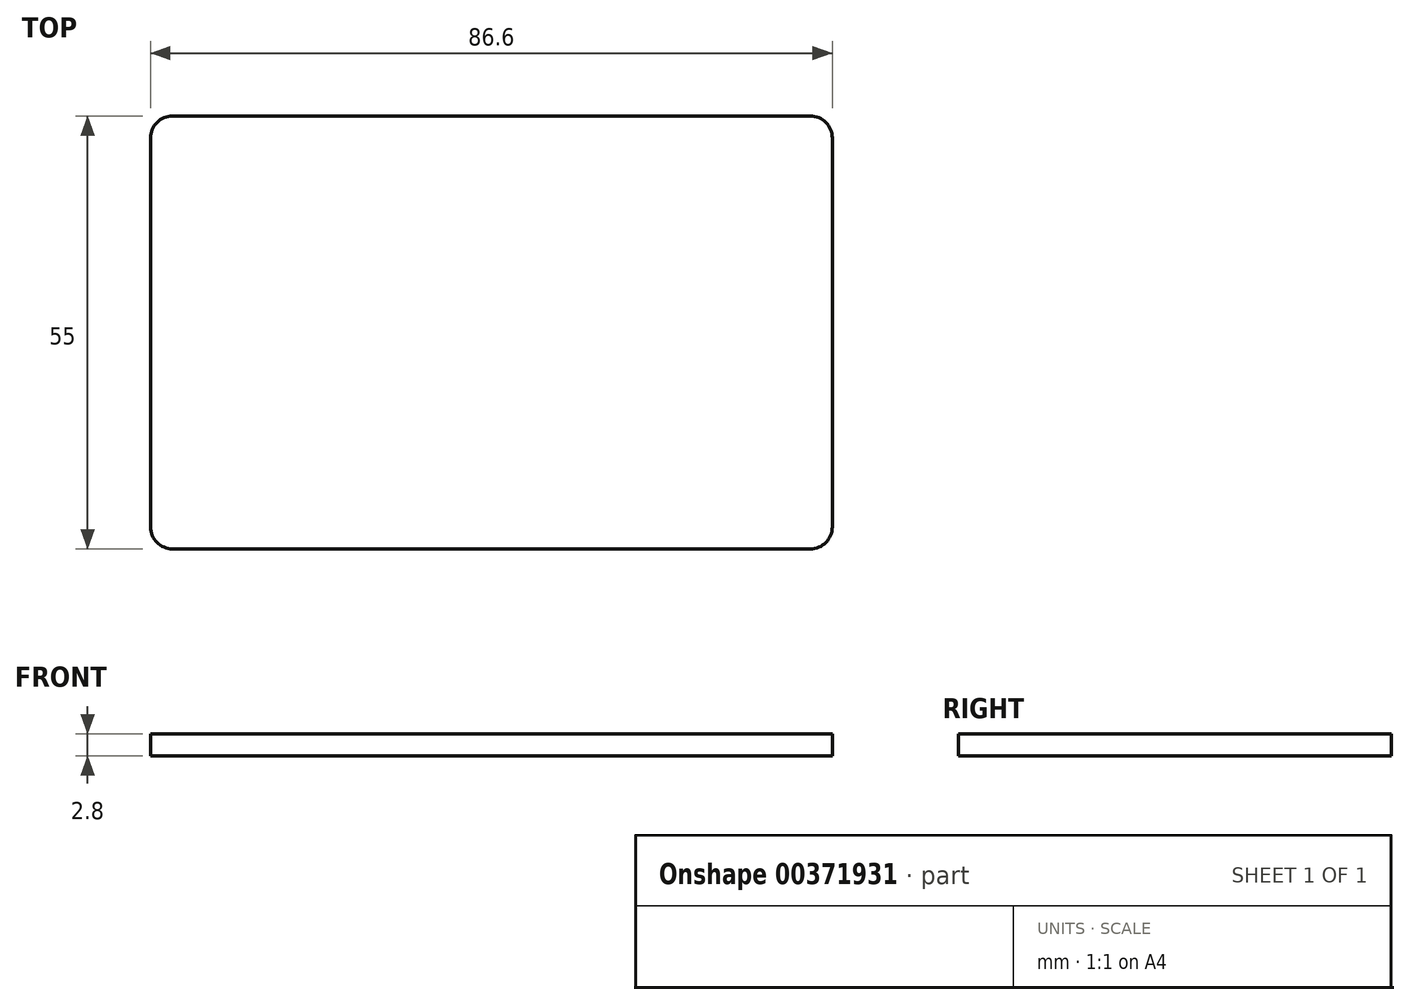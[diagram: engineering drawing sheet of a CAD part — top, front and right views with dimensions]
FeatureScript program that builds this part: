
annotation { "Feature Type Name" : "Feature", "Feature Type Description" : "" }
export const myFeature = defineFeature(function(context is Context, id is Id, definition is map)
    precondition{}
    {
        {
            var Q0;
            Q0=qCreatedBy(makeId("Top.planeOp"),FACE);
            var sketch = newSketch(context, id + "F0", { "sketchPlane" : qUnion([Q0])});
            skLineSegment(sketch, "E0.bottom", {"start": v(-43.3, 27.5) * mm, "end": v(43.3, 27.5) * mm});
            skLineSegment(sketch, "E0.top", {"start": v(-43.3, -27.5) * mm, "end": v(43.3, -27.5) * mm});
            skLineSegment(sketch, "E0.left", {"start": v(-43.3, 27.5) * mm, "end": v(-43.3, -27.5) * mm});
            skLineSegment(sketch, "E0.right", {"start": v(43.3, 27.5) * mm, "end": v(43.3, -27.5) * mm});
            skPoint(sketch, "E0.middle", {"position": v(0, 0) * mm});
            skSolve(sketch);
        }
        {
            var Q0;
            Q0=qSketchRegion(id+"F0",true);
            extrude(context, id + "F1", {"entities" : qUnion([Q0]), "depth" : 2.8 * mm});
        }
        {
            var Q0;
            Q0=makeQuery(id+"F1.opExtrude","SWEPT_EDGE",EDGE,{"disambiguationData":[OSD([sQuery(id+"F0.wireOp",EDGE,"E0.top"),sQuery(id+"F0.wireOp",EDGE,"E0.left")])]});
            var Q1;
            Q1=makeQuery(id+"F1.opExtrude","SWEPT_EDGE",EDGE,{"disambiguationData":[OSD([sQuery(id+"F0.wireOp",EDGE,"E0.bottom"),sQuery(id+"F0.wireOp",EDGE,"E0.left")])]});
            var Q2;
            Q2=makeQuery(id+"F1.opExtrude","SWEPT_EDGE",EDGE,{"disambiguationData":[OSD([sQuery(id+"F0.wireOp",EDGE,"E0.top"),sQuery(id+"F0.wireOp",EDGE,"E0.right")])]});
            var Q3;
            Q3=makeQuery(id+"F1.opExtrude","SWEPT_EDGE",EDGE,{"disambiguationData":[OSD([sQuery(id+"F0.wireOp",EDGE,"E0.bottom"),sQuery(id+"F0.wireOp",EDGE,"E0.right")])]});
            fillet(context, id + "F2", {"entities" : qUnion([Q0, Q1, Q2, Q3]), "radius" : 2.8 * mm, "tangentPropagation" : true, "allowEdgeOverflow" : false});
        }
    });
